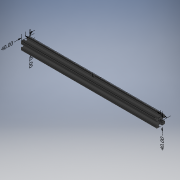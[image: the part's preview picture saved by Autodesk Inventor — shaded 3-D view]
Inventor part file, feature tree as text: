
AUTODESK INVENTOR PART (.ipt)
format: ipt  version: 2019 (Build 230136000, 136)  size: 274,944 bytes
history: native  units: mm
features: other x125, extrude x1, sketch x1
ambient origin geometry x8: Origin, YZ Plane, XZ Plane, XY Plane, X Axis, Y Axis, Z Axis, Center Point
bodies: Solid1 (feature_tree)
feature tree (127):
  other  "Annotations"
  extrude  "Extrusion1"  [1 undecoded]
  other  "CS_ANBAU_HINTEN_LINKS_XY"
  other  "CS_ANBAU_HINTEN_LINKS_YZ"
  other  "CS_ANBAU_HINTEN_LINKS_ZX"
  other  "CS_ANBAU_HINTEN_LINKS_X"
  other  "CS_ANBAU_HINTEN_LINKS_Y"
  other  "CS_ANBAU_HINTEN_LINKS_Z"
  other  "CS_ANBAU_HINTEN_LINKS_Center"
  other  "CS_ANBAU_HINTEN_OBEN_XY"
  other  "CS_ANBAU_HINTEN_OBEN_YZ"
  other  "CS_ANBAU_HINTEN_OBEN_ZX"
  other  "CS_ANBAU_HINTEN_OBEN_X"
  other  "CS_ANBAU_HINTEN_OBEN_Y"
  other  "CS_ANBAU_HINTEN_OBEN_Z"
  other  "CS_ANBAU_HINTEN_OBEN_Center"
  other  "CS_ANBAU_HINTEN_RECHTS_XY"
  other  "CS_ANBAU_HINTEN_RECHTS_YZ"
  other  "CS_ANBAU_HINTEN_RECHTS_ZX"
  other  "CS_ANBAU_HINTEN_RECHTS_X"
  other  "CS_ANBAU_HINTEN_RECHTS_Y"
  other  "CS_ANBAU_HINTEN_RECHTS_Z"
  other  "CS_ANBAU_HINTEN_RECHTS_Center"
  other  "CS_ANBAU_HINTEN_UNTEN_XY"
  other  "CS_ANBAU_HINTEN_UNTEN_YZ"
  other  "CS_ANBAU_HINTEN_UNTEN_ZX"
  other  "CS_ANBAU_HINTEN_UNTEN_X"
  other  "CS_ANBAU_HINTEN_UNTEN_Y"
  other  "CS_ANBAU_HINTEN_UNTEN_Z"
  other  "CS_ANBAU_HINTEN_UNTEN_Center"
  other  "CS_ANBAU_QUER_XY"
  other  "CS_ANBAU_QUER_YZ"
  other  "CS_ANBAU_QUER_ZX"
  other  "CS_ANBAU_QUER_X"
  other  "CS_ANBAU_QUER_Y"
  other  "CS_ANBAU_QUER_Z"
  other  "CS_ANBAU_QUER_Center"
  other  "CS_ANBAU_QUER_1_XY"
  other  "CS_ANBAU_QUER_1_YZ"
  other  "CS_ANBAU_QUER_1_ZX"
  other  "CS_ANBAU_QUER_1_X"
  other  "CS_ANBAU_QUER_1_Y"
  other  "CS_ANBAU_QUER_1_Z"
  other  "CS_ANBAU_QUER_1_Center"
  other  "CS_ANBAU_VORNE_LINKS_XY"
  other  "CS_ANBAU_VORNE_LINKS_YZ"
  other  "CS_ANBAU_VORNE_LINKS_ZX"
  other  "CS_ANBAU_VORNE_LINKS_X"
  other  "CS_ANBAU_VORNE_LINKS_Y"
  other  "CS_ANBAU_VORNE_LINKS_Z"
  other  "CS_ANBAU_VORNE_LINKS_Center"
  other  "CS_ANBAU_VORNE_OBEN_XY"
  other  "CS_ANBAU_VORNE_OBEN_YZ"
  other  "CS_ANBAU_VORNE_OBEN_ZX"
  other  "CS_ANBAU_VORNE_OBEN_X"
  other  "CS_ANBAU_VORNE_OBEN_Y"
  other  "CS_ANBAU_VORNE_OBEN_Z"
  other  "CS_ANBAU_VORNE_OBEN_Center"
  other  "CS_ANBAU_VORNE_RECHTS_XY"
  other  "CS_ANBAU_VORNE_RECHTS_YZ"
  other  "CS_ANBAU_VORNE_RECHTS_ZX"
  other  "CS_ANBAU_VORNE_RECHTS_X"
  other  "CS_ANBAU_VORNE_RECHTS_Y"
  other  "CS_ANBAU_VORNE_RECHTS_Z"
  other  "CS_ANBAU_VORNE_RECHTS_Center"
  other  "CS_ANBAU_VORNE_UNTEN_XY"
  other  "CS_ANBAU_VORNE_UNTEN_YZ"
  other  "CS_ANBAU_VORNE_UNTEN_ZX"
  other  "CS_ANBAU_VORNE_UNTEN_X"
  other  "CS_ANBAU_VORNE_UNTEN_Y"
  other  "CS_ANBAU_VORNE_UNTEN_Z"
  other  "CS_ANBAU_VORNE_UNTEN_Center"
  other  "p1_XY"
  other  "p1_YZ"
  other  "p1_ZX"
  other  "p1_X"
  other  "p1_Y"
  other  "p1_Z"
  other  "p1_Center"
  other  "p2_XY"
  other  "p2_YZ"
  other  "p2_ZX"
  other  "p2_X"
  other  "p2_Y"
  other  "p2_Z"
  other  "p2_Center"
  other  "p3_XY"
  other  "p3_YZ"
  other  "p3_ZX"
  other  "p3_X"
  other  "p3_Y"
  other  "p3_Z"
  other  "p3_Center"
  other  "p4_XY"
  other  "p4_YZ"
  other  "p4_ZX"
  other  "p4_X"
  other  "p4_Y"
  other  "p4_Z"
  other  "p4_Center"
  other  "p5_XY"
  other  "p5_YZ"
  other  "p5_ZX"
  other  "p5_X"
  other  "p5_Y"
  other  "p5_Z"
  other  "p5_Center"
  other  "pm1_XY"
  other  "pm1_YZ"
  other  "pm1_ZX"
  other  "pm1_X"
  other  "pm1_Y"
  other  "pm1_Z"
  other  "pm1_Center"
  other  "pm2_XY"
  other  "pm2_YZ"
  other  "pm2_ZX"
  other  "pm2_X"
  other  "pm2_Y"
  other  "pm2_Z"
  other  "pm2_Center"
  sketch  "Skizze_1"  dims[d0=670.0mm d1=0.0mm d2=0.0mm d3=0.0mm d4=0.0mm d5=0.0mm d6=0.0mm d10=670.0mm d11=670.0mm d7=40.0mm d8=40.0mm d9=40.0mm]
  other  "Linear Dimension 1"
  other  "Linear Dimension 2"
  other  "Linear Dimension 3"
  other  "Linear Dimension 4"
  other  "Linear Dimension 5"
note: 1 required parameter value undecoded (feature->parameter linkage not recoverable at this tier; creation-order binding heuristic only, values carry confidence <= 0.55)
